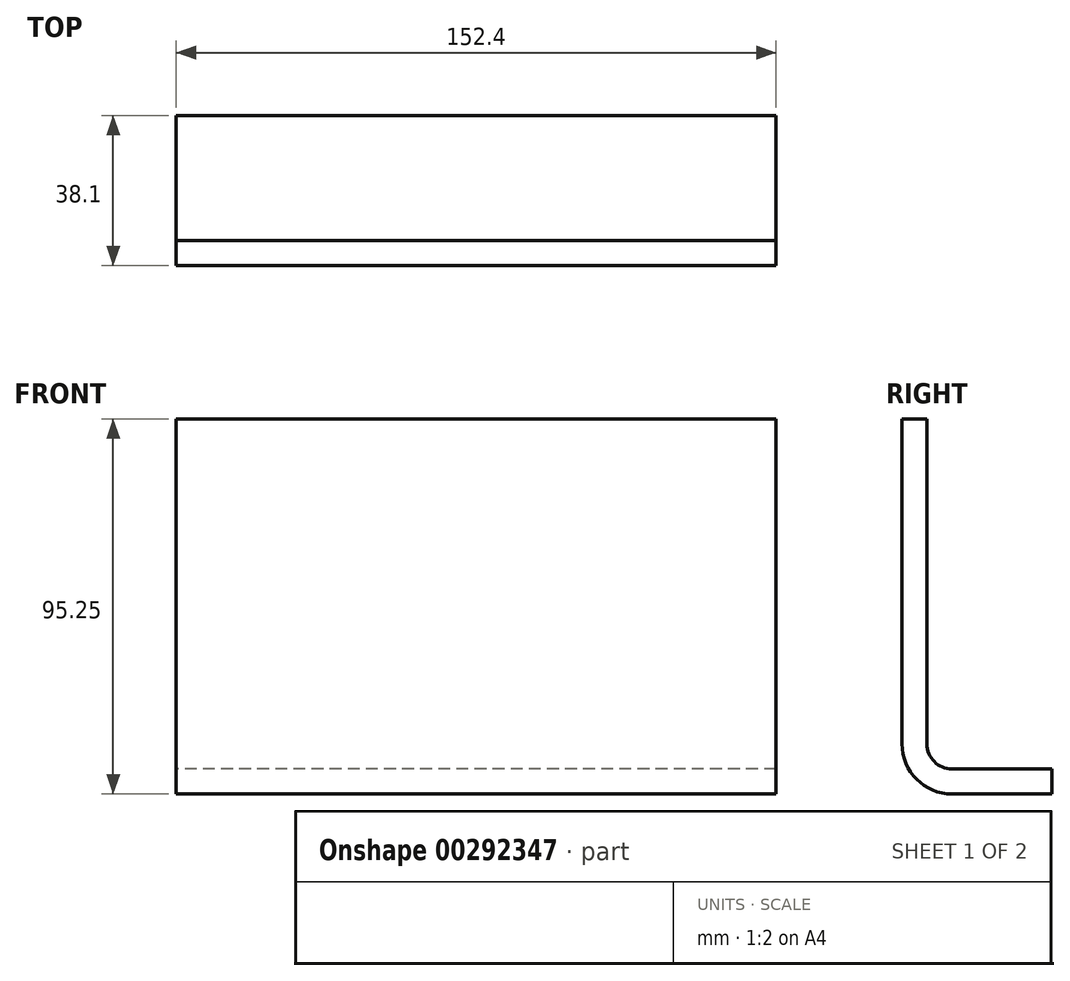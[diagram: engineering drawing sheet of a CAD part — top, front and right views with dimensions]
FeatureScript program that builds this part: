
annotation { "Feature Type Name" : "Feature", "Feature Type Description" : "" }
export const myFeature = defineFeature(function(context is Context, id is Id, definition is map)
    precondition{}
    {
        {
            var Q0;
            Q0=qCreatedBy(makeId("Right.planeOp"),FACE);
            var sketch = newSketch(context, id + "F0", { "sketchPlane" : qUnion([Q0])});
            skLineSegment(sketch, "E0", {"start": v(-6.35, -6.35) * mm, "end": v(-6.35, 88.9) * mm});
            skLineSegment(sketch, "E1", {"start": v(-6.35, -6.35) * mm, "end": v(31.75, -6.35) * mm});
            skLineSegment(sketch, "E2.0", {"start": v(0, 0) * mm, "end": v(0, 88.9) * mm});
            skLineSegment(sketch, "E3.0", {"start": v(0, 0) * mm, "end": v(31.75, 0) * mm});
            skLineSegment(sketch, "E4", {"start": v(31.75, -6.35) * mm, "end": v(31.75, 0) * mm});
            skLineSegment(sketch, "E5", {"start": v(-6.35, 88.9) * mm, "end": v(0, 88.9) * mm});
            skSolve(sketch);
        }
        {
            var Q0;
            Q0=makeQuery(id+"F0.imprint","IMPRINT",FACE,{"disambiguationData":[TD([[makeQuery(id+"F0.imprint","IMPRINT",EDGE,{"derivedFrom":sQuery(id+"F0.wireOp",EDGE,"E0")}),-1.0]])]});
            extrude(context, id + "F1", {"entities" : qUnion([Q0]), "endBound" : BoundingType.SYMMETRIC, "depth" : 152.4 * mm});
        }
        {
            var Q0;
            Q0=makeQuery(id+"F1.opExtrude","SWEPT_EDGE",EDGE,{"disambiguationData":[OSD([sQuery(id+"F0.wireOp",EDGE,"E2.0"),sQuery(id+"F0.wireOp",EDGE,"E3.0")])]});
            fillet(context, id + "F2", {"entities" : qUnion([Q0]), "radius" : 6.35 * mm, "tangentPropagation" : true, "allowEdgeOverflow" : false});
        }
        {
            var Q0;
            Q0=makeQuery(id+"F1.opExtrude","SWEPT_EDGE",EDGE,{"disambiguationData":[OSD([sQuery(id+"F0.wireOp",EDGE,"E0"),sQuery(id+"F0.wireOp",EDGE,"E1")])]});
            fillet(context, id + "F3", {"entities" : qUnion([Q0]), "radius" : 12.7 * mm, "tangentPropagation" : true, "allowEdgeOverflow" : false});
        }
    });
